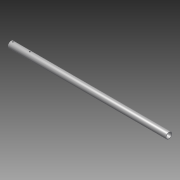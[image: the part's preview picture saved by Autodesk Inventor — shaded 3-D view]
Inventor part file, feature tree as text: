
AUTODESK INVENTOR PART (.ipt)
format: ipt  version: 2014 (Build 180170000, 170)  size: 124,928 bytes
history: native  units: in
note: dims shown in document units (in); Inventor stores cm internally (conversion verified against a paired STEP export)
features: other x2, extrude x2, sketch x2, plane x1, imported_body x1, projected_geometry x1
ambient origin geometry x8: Origin, YZ Plane, XZ Plane, XY Plane, X Axis, Y Axis, Z Axis, Center Point
bodies: Body1 (feature_tree)
feature tree (9):
  parser-record x1  (decoder bookkeeping rows leaked as tree rows — omitted from the tree; the rows remain in map.json)
  other  "4347K3111"
  extrude  "Extrusion1"  Depth=0.19in
  plane  "Work Plane1"
  extrude  "Extrusion2"  Depth=2.5in
  imported_body  "Base1"
  sketch  "Sketch1"  dims[d0=9.0in d1=0.0in d2=0.19in]
  sketch  "Sketch2"  dims[d3=0.25in d4=2.5in d5=1.0in d6=0.0in]
  projected_geometry  "Projected Loop1"
